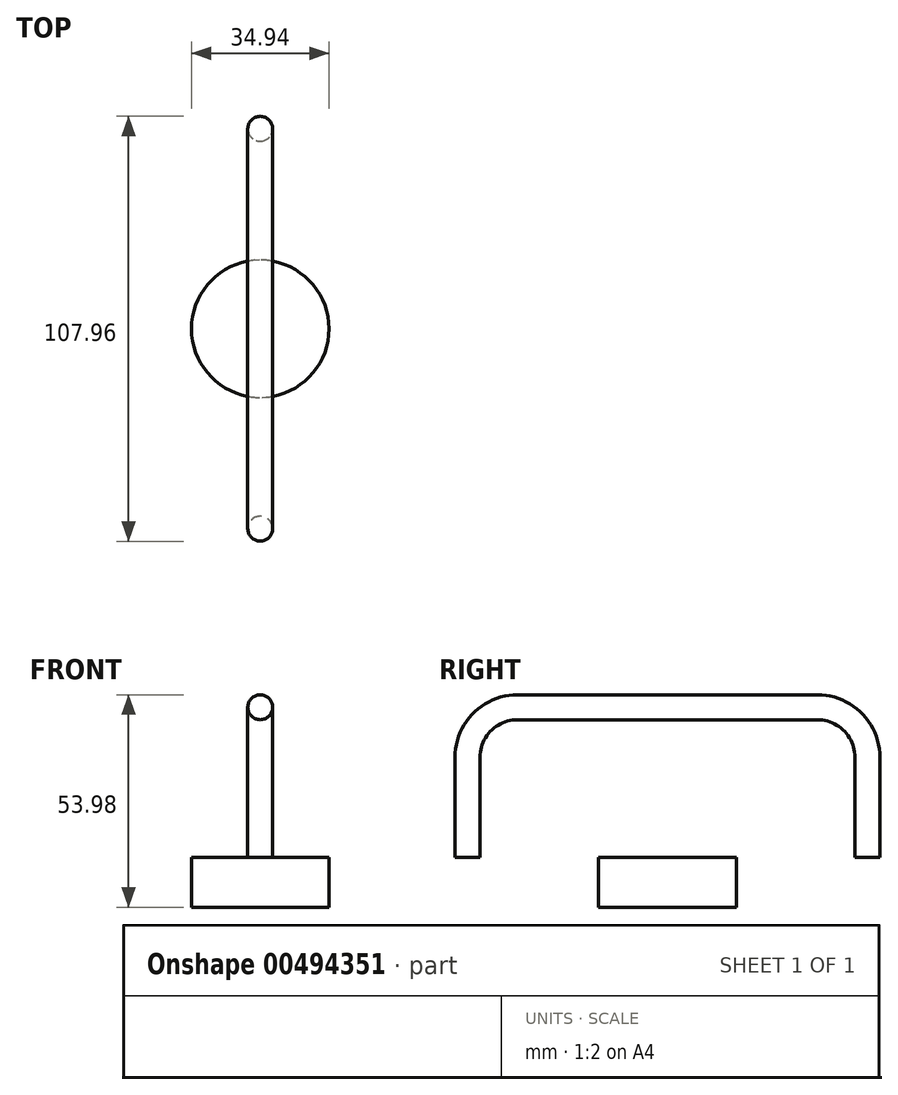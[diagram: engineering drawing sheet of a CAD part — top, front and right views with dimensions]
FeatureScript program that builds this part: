
annotation { "Feature Type Name" : "Feature", "Feature Type Description" : "" }
export const myFeature = defineFeature(function(context is Context, id is Id, definition is map)
    precondition{}
    {
        {
            var Q0;
            Q0=qCreatedBy(makeId("Top.planeOp"),FACE);
            var sketch = newSketch(context, id + "F0", { "sketchPlane" : qUnion([Q0])});
            skCircle(sketch, "E0", {"center": v(0, -50.8) * mm, "radius": 3.18 * mm});
            skCircle(sketch, "E1", {"center": v(0, 50.8) * mm, "radius": 3.17 * mm});
            skLineSegment(sketch, "E2", {"start": v(0, 50.8) * mm, "end": v(0, -50.8) * mm, "construction": true});
            skPoint(sketch, "E3", {"position": v(0, 0) * mm});
            skSolve(sketch);
        }
        {
            var Q0;
            Q0=qCreatedBy(makeId("Right.planeOp"),FACE);
            var sketch = newSketch(context, id + "F1", { "sketchPlane" : qUnion([Q0])});
            skPoint(sketch, "E4.0", {"position": v(-50.8, 0) * mm});
            skPoint(sketch, "E5.0", {"position": v(50.8, 0) * mm});
            skLineSegment(sketch, "E6", {"start": v(-50.8, 0) * mm, "end": v(-50.8, 25.4) * mm});
            skLineSegment(sketch, "E7", {"start": v(-38.1, 38.1) * mm, "end": v(38.1, 38.1) * mm});
            skLineSegment(sketch, "E8", {"start": v(50.8, 25.4) * mm, "end": v(50.8, 0) * mm});
            skPoint(sketch, "E9.visualSharp", {"position": v(-50.8, 38.1) * mm});
            skArc(sketch, "E9.filletArc", {"start": v(-38.1, 38.1) * mm, "mid": v(-47.08, 34.38) * mm, "end": v(-50.8, 25.4) * mm});
            skPoint(sketch, "E10.visualSharp", {"position": v(50.8, 38.1) * mm});
            skArc(sketch, "E10.filletArc", {"start": v(50.8, 25.4) * mm, "mid": v(47.08, 34.38) * mm, "end": v(38.1, 38.1) * mm});
            skSolve(sketch);
        }
        {
            var Q0;
            Q0=makeQuery(id+"F0.imprint","IMPRINT",FACE,{"disambiguationData":[TD([[makeQuery(id+"F0.imprint","IMPRINT",EDGE,{"derivedFrom":sQuery(id+"F0.wireOp",EDGE,"E0")}),1.0]])]});
            var Q1;
            Q1=sQuery(id+"F1.wireOp",EDGE,"E6");
            var Q2;
            Q2=sQuery(id+"F1.wireOp",EDGE,"E9.filletArc");
            var Q3;
            Q3=sQuery(id+"F1.wireOp",EDGE,"E7");
            var Q4;
            Q4=sQuery(id+"F1.wireOp",EDGE,"E10.filletArc");
            var Q5;
            Q5=sQuery(id+"F1.wireOp",EDGE,"E8");
            sweep(context, id + "F2", {"profiles" : qUnion([Q0]), "path" : qUnion([Q1, Q2, Q3, Q4, Q5])});
        }
        {
            var Q0;
            Q0=qCreatedBy(makeId("Top.planeOp"),FACE);
            var sketch = newSketch(context, id + "F3", { "sketchPlane" : qUnion([Q0])});
            skCircle(sketch, "E11", {"center": v(0, 0) * mm, "radius": 17.47 * mm});
            skSolve(sketch);
        }
        {
            var Q0;
            Q0=makeQuery(id+"F3.imprint","IMPRINT",FACE,{"disambiguationData":[TD([[makeQuery(id+"F3.imprint","IMPRINT",EDGE,{"derivedFrom":sQuery(id+"F3.wireOp",EDGE,"E11")}),1.0]])]});
            extrude(context, id + "F4", {"entities" : qUnion([Q0]), "oppositeDirection" : true, "depth" : 12.7 * mm});
        }
    });
